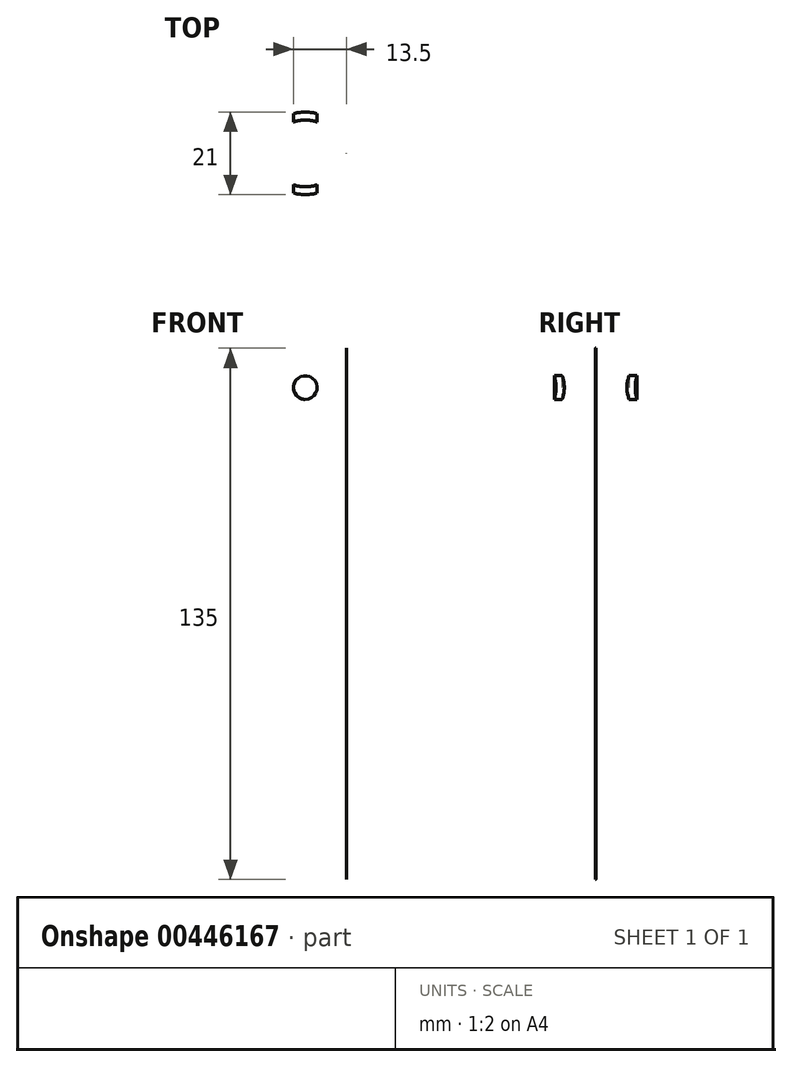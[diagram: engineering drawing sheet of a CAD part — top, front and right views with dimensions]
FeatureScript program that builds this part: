
annotation { "Feature Type Name" : "Feature", "Feature Type Description" : "" }
export const myFeature = defineFeature(function(context is Context, id is Id, definition is map)
    precondition{}
    {
        {
            var Q0;
            Q0=qCreatedBy(makeId("Top.planeOp"),FACE);
            var sketch = newSketch(context, id + "F0", { "sketchPlane" : qUnion([Q0])});
            skCircle(sketch, "E0", {"center": v(0, 0) * mm, "radius": 8.5 * mm});
            skCircle(sketch, "E1", {"center": v(0, 0) * mm, "radius": 9.5 * mm});
            skCircle(sketch, "E2", {"center": v(0, 0) * mm, "radius": 9.7 * mm});
            skCircle(sketch, "E3", {"center": v(0, 0) * mm, "radius": 10.5 * mm});
            skSolve(sketch);
        }
        {
            var Q0;
            Q0=qCreatedBy(makeId("Front.planeOp"),FACE);
            var sketch = newSketch(context, id + "F1", { "sketchPlane" : qUnion([Q0])});
            skLineSegment(sketch, "E4.bottom", {"start": v(-10.5, -25) * mm, "end": v(10.5, -25) * mm});
            skLineSegment(sketch, "E4.top", {"start": v(-10.5, 115) * mm, "end": v(10.5, 115) * mm});
            skLineSegment(sketch, "E4.left", {"start": v(-10.5, -25) * mm, "end": v(-10.5, 115) * mm});
            skLineSegment(sketch, "E4.right", {"start": v(10.5, -25) * mm, "end": v(10.5, 115) * mm});
            skLineSegment(sketch, "E5", {"start": v(0, -25) * mm, "end": v(0, 115) * mm});
            skCircle(sketch, "E6", {"center": v(0, 105) * mm, "radius": 3 * mm});
            skCircle(sketch, "E7", {"center": v(0, 95) * mm, "radius": 3 * mm});
            skCircle(sketch, "E8", {"center": v(0, 85) * mm, "radius": 3 * mm});
            skSolve(sketch);
        }
        {
            var Q0;
            Q0=makeQuery(id+"F0.imprint","IMPRINT",FACE,{"disambiguationData":[TD([[makeQuery(id+"F0.imprint","IMPRINT",EDGE,{"derivedFrom":sQuery(id+"F0.wireOp",EDGE,"E0")}),-1.0]])]});
            var Q1;
            Q1=makeQuery(id+"F0.imprint","IMPRINT",FACE,{"disambiguationData":[TD([[makeQuery(id+"F0.imprint","IMPRINT",EDGE,{"derivedFrom":sQuery(id+"F0.wireOp",EDGE,"E1")}),-1.0]])]});
            var Q2;
            Q2=makeQuery(id+"F0.imprint","IMPRINT",FACE,{"disambiguationData":[TD([[makeQuery(id+"F0.imprint","IMPRINT",EDGE,{"derivedFrom":sQuery(id+"F0.wireOp",EDGE,"E2")}),-1.0]])]});
            extrude(context, id + "F2", {"entities" : qUnion([Q0, Q1, Q2]), "depth" : 115 * mm});
        }
        {
            var Q0;
            Q0=makeQuery(id+"F0.imprint","IMPRINT",FACE,{"disambiguationData":[TD([[makeQuery(id+"F0.imprint","IMPRINT",EDGE,{"derivedFrom":sQuery(id+"F0.wireOp",EDGE,"E2")}),-1.0]])]});
            extrude(context, id + "F3", {"entities" : qUnion([Q0]), "operationType" : NewBodyOperationType.ADD, "oppositeDirection" : true, "depth" : 20 * mm});
        }
        {
            var Q0;
            {var subQ0=sQuery(id+"F1.wireOp",EDGE,"E8");var subQ1=sQuery(id+"F1.wireOp",EDGE,"E5");var subQ2=makeQuery(id+"F1.imprint","INTERSECT",VERTEX,{"disambiguationData":[OD(0.0)],"derivedFrom":[subQ1,subQ0]});Q0=makeQuery(id+"F1.imprint","IMPRINT",FACE,{"disambiguationData":[TD([[makeQuery(id+"F1.imprint","IMPRINT",EDGE,{"disambiguationData":[TD([[subQ2,-1.0]])],"derivedFrom":subQ1}),-1.0]])]});}
            var Q1;
            {var subQ0=sQuery(id+"F1.wireOp",EDGE,"E8");var subQ1=sQuery(id+"F1.wireOp",EDGE,"E5");var subQ2=makeQuery(id+"F1.imprint","INTERSECT",VERTEX,{"disambiguationData":[OD(0.0)],"derivedFrom":[subQ1,subQ0]});Q1=makeQuery(id+"F1.imprint","IMPRINT",FACE,{"disambiguationData":[TD([[makeQuery(id+"F1.imprint","IMPRINT",EDGE,{"disambiguationData":[TD([[subQ2,-1.0]])],"derivedFrom":subQ1}),1.0]])]});}
            var Q2;
            {var subQ0=sQuery(id+"F1.wireOp",EDGE,"E7");var subQ1=sQuery(id+"F1.wireOp",EDGE,"E5");var subQ2=makeQuery(id+"F1.imprint","INTERSECT",VERTEX,{"disambiguationData":[OD(0.0)],"derivedFrom":[subQ1,subQ0]});Q2=makeQuery(id+"F1.imprint","IMPRINT",FACE,{"disambiguationData":[TD([[makeQuery(id+"F1.imprint","IMPRINT",EDGE,{"disambiguationData":[TD([[subQ2,-1.0]])],"derivedFrom":subQ1}),1.0]])]});}
            var Q3;
            {var subQ0=sQuery(id+"F1.wireOp",EDGE,"E7");var subQ1=sQuery(id+"F1.wireOp",EDGE,"E5");var subQ2=makeQuery(id+"F1.imprint","INTERSECT",VERTEX,{"disambiguationData":[OD(0.0)],"derivedFrom":[subQ1,subQ0]});Q3=makeQuery(id+"F1.imprint","IMPRINT",FACE,{"disambiguationData":[TD([[makeQuery(id+"F1.imprint","IMPRINT",EDGE,{"disambiguationData":[TD([[subQ2,-1.0]])],"derivedFrom":subQ1}),-1.0]])]});}
            var Q4;
            {var subQ0=sQuery(id+"F1.wireOp",EDGE,"E6");var subQ1=sQuery(id+"F1.wireOp",EDGE,"E5");var subQ2=makeQuery(id+"F1.imprint","INTERSECT",VERTEX,{"disambiguationData":[OD(0.0)],"derivedFrom":[subQ1,subQ0]});Q4=makeQuery(id+"F1.imprint","IMPRINT",FACE,{"disambiguationData":[TD([[makeQuery(id+"F1.imprint","IMPRINT",EDGE,{"disambiguationData":[TD([[subQ2,-1.0]])],"derivedFrom":subQ1}),-1.0]])]});}
            var Q5;
            {var subQ0=sQuery(id+"F1.wireOp",EDGE,"E6");var subQ1=sQuery(id+"F1.wireOp",EDGE,"E5");var subQ2=makeQuery(id+"F1.imprint","INTERSECT",VERTEX,{"disambiguationData":[OD(0.0)],"derivedFrom":[subQ1,subQ0]});Q5=makeQuery(id+"F1.imprint","IMPRINT",FACE,{"disambiguationData":[TD([[makeQuery(id+"F1.imprint","IMPRINT",EDGE,{"disambiguationData":[TD([[subQ2,-1.0]])],"derivedFrom":subQ1}),1.0]])]});}
            extrude(context, id + "F4", {"entities" : qUnion([Q0, Q1, Q2, Q3, Q4, Q5]), "operationType" : NewBodyOperationType.REMOVE, "endBound" : BoundingType.SYMMETRIC, "oppositeDirection" : true, "depth" : 25 * mm});
        }
    });
